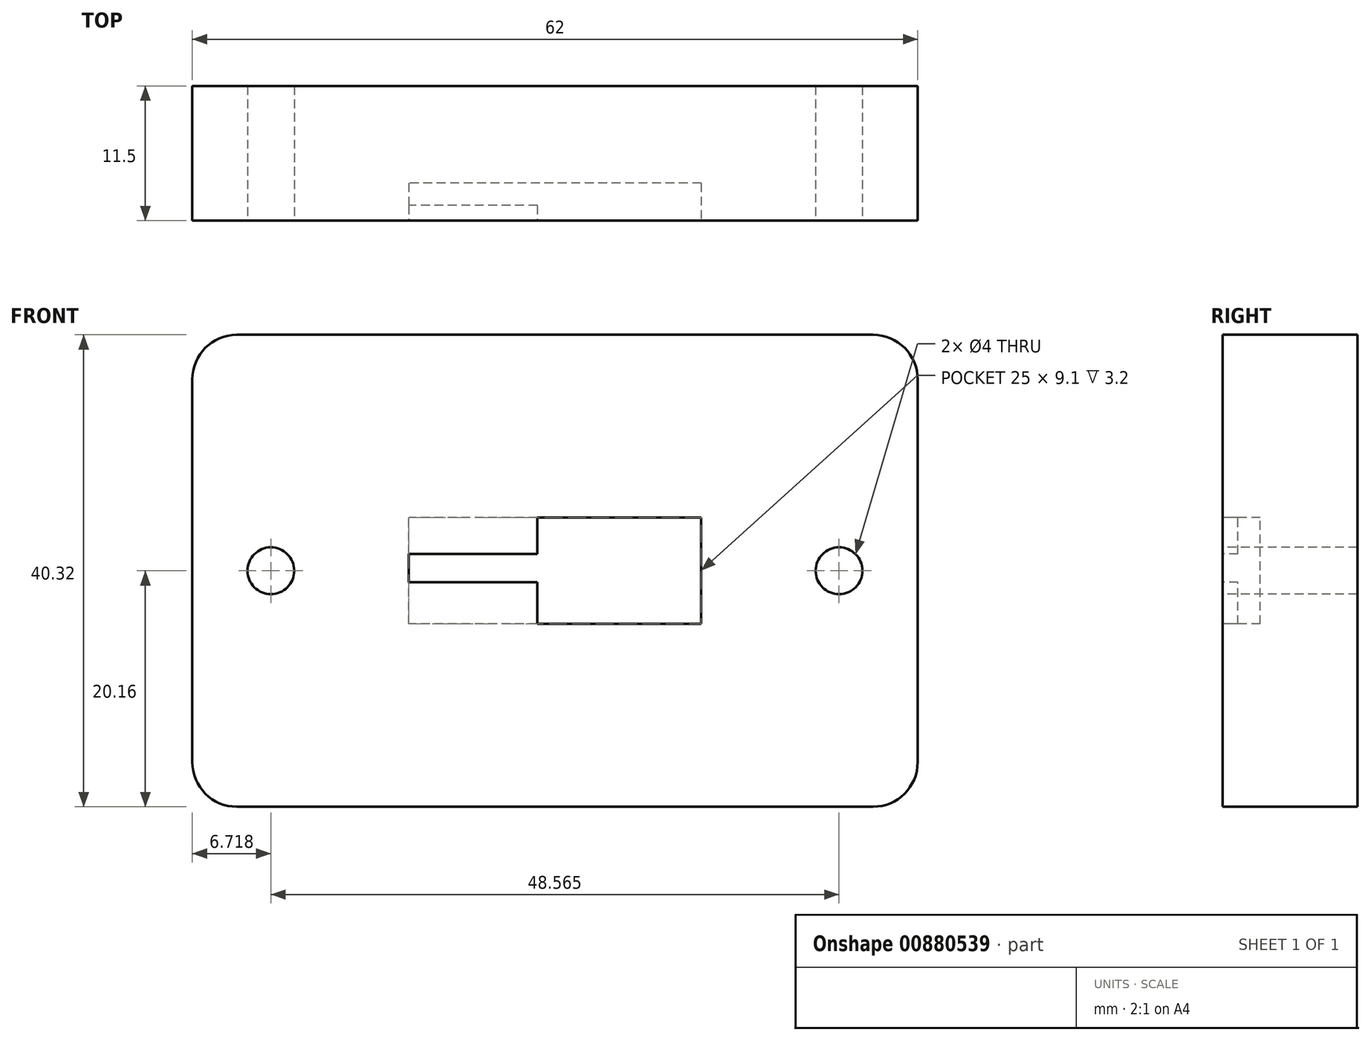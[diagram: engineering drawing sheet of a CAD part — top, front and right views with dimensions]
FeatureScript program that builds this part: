
annotation { "Feature Type Name" : "Feature", "Feature Type Description" : "" }
export const myFeature = defineFeature(function(context is Context, id is Id, definition is map)
    precondition{}
    {
        {
            var Q0;
            Q0=qCreatedBy(makeId("Front.planeOp"),FACE);
            var sketch = newSketch(context, id + "F0", { "sketchPlane" : qUnion([Q0])});
            skLineSegment(sketch, "E0.bottom", {"start": v(31, -20.16) * mm, "end": v(-31, -20.16) * mm});
            skLineSegment(sketch, "E0.top", {"start": v(31, 20.16) * mm, "end": v(-31, 20.16) * mm});
            skLineSegment(sketch, "E0.left", {"start": v(31, -20.16) * mm, "end": v(31, 20.16) * mm});
            skLineSegment(sketch, "E0.right", {"start": v(-31, -20.16) * mm, "end": v(-31, 20.16) * mm});
            skPoint(sketch, "E0.middle", {"position": v(0, 0) * mm});
            skSolve(sketch);
        }
        {
            var Q0;
            Q0 = qSketchRegion(id + "F0", true);
            extrude(context, id + "F1", {"entities" : qUnion([Q0]), "depth" : 11.5 * mm, "offsetDistance" : 25.4 * mm});
        }
        {
            var Q0;
            Q0=makeQuery(id+"F1.opExtrude","CAP_FACE",FACE,{"disambiguationData":[OSD([sQuery(id+"F0.wireOp",EDGE,"E0.bottom"),sQuery(id+"F0.wireOp",EDGE,"E0.top"),sQuery(id+"F0.wireOp",EDGE,"E0.left"),sQuery(id+"F0.wireOp",EDGE,"E0.right")])],"isStart":false});
            var sketch = newSketch(context, id + "F2", { "sketchPlane" : qUnion([Q0])});
            skLineSegment(sketch, "E1.bottom", {"start": v(12.5, -4.55) * mm, "end": v(-12.5, -4.55) * mm});
            skLineSegment(sketch, "E1.top", {"start": v(12.5, 4.55) * mm, "end": v(-12.5, 4.55) * mm});
            skLineSegment(sketch, "E1.left", {"start": v(12.5, -4.55) * mm, "end": v(12.5, 4.55) * mm});
            skLineSegment(sketch, "E1.right", {"start": v(-12.5, -4.55) * mm, "end": v(-12.5, 4.55) * mm});
            skPoint(sketch, "E1.middle", {"position": v(0, 0) * mm});
            skSolve(sketch);
        }
        {
            var Q0;
            Q0 = qSketchRegion(id + "F2", true);
            extrude(context, id + "F3", {"entities" : qUnion([Q0]), "operationType" : NewBodyOperationType.REMOVE, "oppositeDirection" : true, "depth" : 3.2 * mm, "offsetDistance" : 25.4 * mm});
        }
        {
            var Q0;
            Q0=makeQuery(id+"F1.opExtrude","CAP_FACE",FACE,{"disambiguationData":[OSD([sQuery(id+"F0.wireOp",EDGE,"E0.bottom"),sQuery(id+"F0.wireOp",EDGE,"E0.top"),sQuery(id+"F0.wireOp",EDGE,"E0.left"),sQuery(id+"F0.wireOp",EDGE,"E0.right")])],"isStart":false});
            var sketch = newSketch(context, id + "F4", { "sketchPlane" : qUnion([Q0])});
            skLineSegment(sketch, "E2.bottom", {"start": v(-12.5, 4.55) * mm, "end": v(-1.5, 4.55) * mm});
            skLineSegment(sketch, "E2.top", {"start": v(-12.5, 1.44) * mm, "end": v(-1.5, 1.44) * mm});
            skLineSegment(sketch, "E2.left", {"start": v(-12.5, 4.55) * mm, "end": v(-12.5, 1.44) * mm});
            skLineSegment(sketch, "E2.right", {"start": v(-1.5, 4.55) * mm, "end": v(-1.5, 1.44) * mm});
            skLineSegment(sketch, "E3.bottom", {"start": v(-12.5, -0.96) * mm, "end": v(-1.5, -0.96) * mm});
            skLineSegment(sketch, "E3.top", {"start": v(-12.5, -4.55) * mm, "end": v(-1.5, -4.55) * mm});
            skLineSegment(sketch, "E3.left", {"start": v(-12.5, -0.96) * mm, "end": v(-12.5, -4.55) * mm});
            skLineSegment(sketch, "E3.right", {"start": v(-1.5, -0.96) * mm, "end": v(-1.5, -4.55) * mm});
            skLineSegment(sketch, "E4.left", {"start": v(-12.5, 1.44) * mm, "end": v(-12.5, -0.96) * mm});
            skLineSegment(sketch, "E4.right", {"start": v(-1.5, 1.44) * mm, "end": v(-1.5, -0.96) * mm});
            skSolve(sketch);
        }
        {
            var Q0;
            Q0=makeQuery(id+"F4.imprint","IMPRINT",FACE,{"disambiguationData":[TD([[makeQuery(id+"F4.imprint","IMPRINT",EDGE,{"derivedFrom":sQuery(id+"F4.wireOp",EDGE,"E2.bottom")}),1.0]])]});
            var Q1;
            Q1=makeQuery(id+"F4.imprint","IMPRINT",FACE,{"disambiguationData":[TD([[makeQuery(id+"F4.imprint","IMPRINT",EDGE,{"derivedFrom":sQuery(id+"F4.wireOp",EDGE,"E3.top")}),-1.0]])]});
            extrude(context, id + "F5", {"entities" : qUnion([Q0, Q1]), "operationType" : NewBodyOperationType.ADD, "oppositeDirection" : true, "depth" : 1.3 * mm, "offsetDistance" : 25.4 * mm});
        }
        {
            var Q0;
            Q0=makeQuery(id+"F1.opExtrude","SWEPT_EDGE",EDGE,{"disambiguationData":[OSD([sQuery(id+"F0.wireOp",EDGE,"E0.top"),sQuery(id+"F0.wireOp",EDGE,"E0.right")])]});
            var Q1;
            Q1=makeQuery(id+"F1.opExtrude","SWEPT_EDGE",EDGE,{"disambiguationData":[OSD([sQuery(id+"F0.wireOp",EDGE,"E0.top"),sQuery(id+"F0.wireOp",EDGE,"E0.left")])]});
            var Q2;
            Q2=makeQuery(id+"F1.opExtrude","SWEPT_EDGE",EDGE,{"disambiguationData":[OSD([sQuery(id+"F0.wireOp",EDGE,"E0.bottom"),sQuery(id+"F0.wireOp",EDGE,"E0.left")])]});
            var Q3;
            Q3=makeQuery(id+"F1.opExtrude","SWEPT_EDGE",EDGE,{"disambiguationData":[OSD([sQuery(id+"F0.wireOp",EDGE,"E0.bottom"),sQuery(id+"F0.wireOp",EDGE,"E0.right")])]});
            fillet(context, id + "F6", {"entities" : qUnion([Q0, Q1, Q2, Q3]), "radius" : 3.8 * mm, "tangentPropagation" : true, "allowEdgeOverflow" : false});
        }
        {
            var Q0;
            Q0=makeQuery(id+"F5.boolean.opBoolean","MERGE",FACE,{"derivedFrom":[makeQuery(id+"F1.opExtrude","CAP_FACE",FACE,{"disambiguationData":[OSD([sQuery(id+"F0.wireOp",EDGE,"E0.bottom"),sQuery(id+"F0.wireOp",EDGE,"E0.top"),sQuery(id+"F0.wireOp",EDGE,"E0.left"),sQuery(id+"F0.wireOp",EDGE,"E0.right")])],"isStart":false}),makeQuery(id+"F5.opExtrude","CAP_FACE",FACE,{"disambiguationData":[OSD([sQuery(id+"F4.wireOp",EDGE,"E2.bottom"),sQuery(id+"F4.wireOp",EDGE,"E2.left"),sQuery(id+"F4.wireOp",EDGE,"E2.right"),sQuery(id+"F4.wireOp",EDGE,"E2.top")])],"isStart":true}),makeQuery(id+"F5.opExtrude","CAP_FACE",FACE,{"disambiguationData":[OSD([sQuery(id+"F4.wireOp",EDGE,"E3.top"),sQuery(id+"F4.wireOp",EDGE,"E3.left"),sQuery(id+"F4.wireOp",EDGE,"E3.right"),sQuery(id+"F4.wireOp",EDGE,"E3.bottom")])],"isStart":true})]});
            var sketch = newSketch(context, id + "F7", { "sketchPlane" : qUnion([Q0])});
            skLineSegment(sketch, "E5.left", {"start": v(24.28, 0) * mm, "end": v(24.28, 0) * mm});
            skLineSegment(sketch, "E5.right", {"start": v(-24.28, 0) * mm, "end": v(-24.28, 0) * mm});
            skPoint(sketch, "E5.middle", {"position": v(0, 0) * mm});
            skCircle(sketch, "E6", {"center": v(-24.28, 0) * mm, "radius": 2 * mm});
            skCircle(sketch, "E7", {"center": v(24.28, 0) * mm, "radius": 2 * mm});
            skSolve(sketch);
        }
        {
            var Q0;
            Q0=makeQuery(id+"F7.imprint","IMPRINT",FACE,{"disambiguationData":[TD([[makeQuery(id+"F7.imprint","IMPRINT",EDGE,{"derivedFrom":sQuery(id+"F7.wireOp",EDGE,"E6")}),1.0]])]});
            var Q1;
            Q1=makeQuery(id+"F7.imprint","IMPRINT",FACE,{"disambiguationData":[TD([[makeQuery(id+"F7.imprint","IMPRINT",EDGE,{"derivedFrom":sQuery(id+"F7.wireOp",EDGE,"E7")}),1.0]])]});
            var Q2;
            Q2=sQuery(id+"F7.wireOp",EDGE,"E6");
            var Q3;
            Q3=sQuery(id+"F7.wireOp",EDGE,"E7");
            extrude(context, id + "F8", {"entities" : qUnion([Q0, Q1]), "operationType" : NewBodyOperationType.REMOVE, "surfaceEntities" : qUnion([Q2, Q3]), "oppositeDirection" : true, "depth" : 15.24 * mm, "offsetDistance" : 25.4 * mm});
        }
    });
